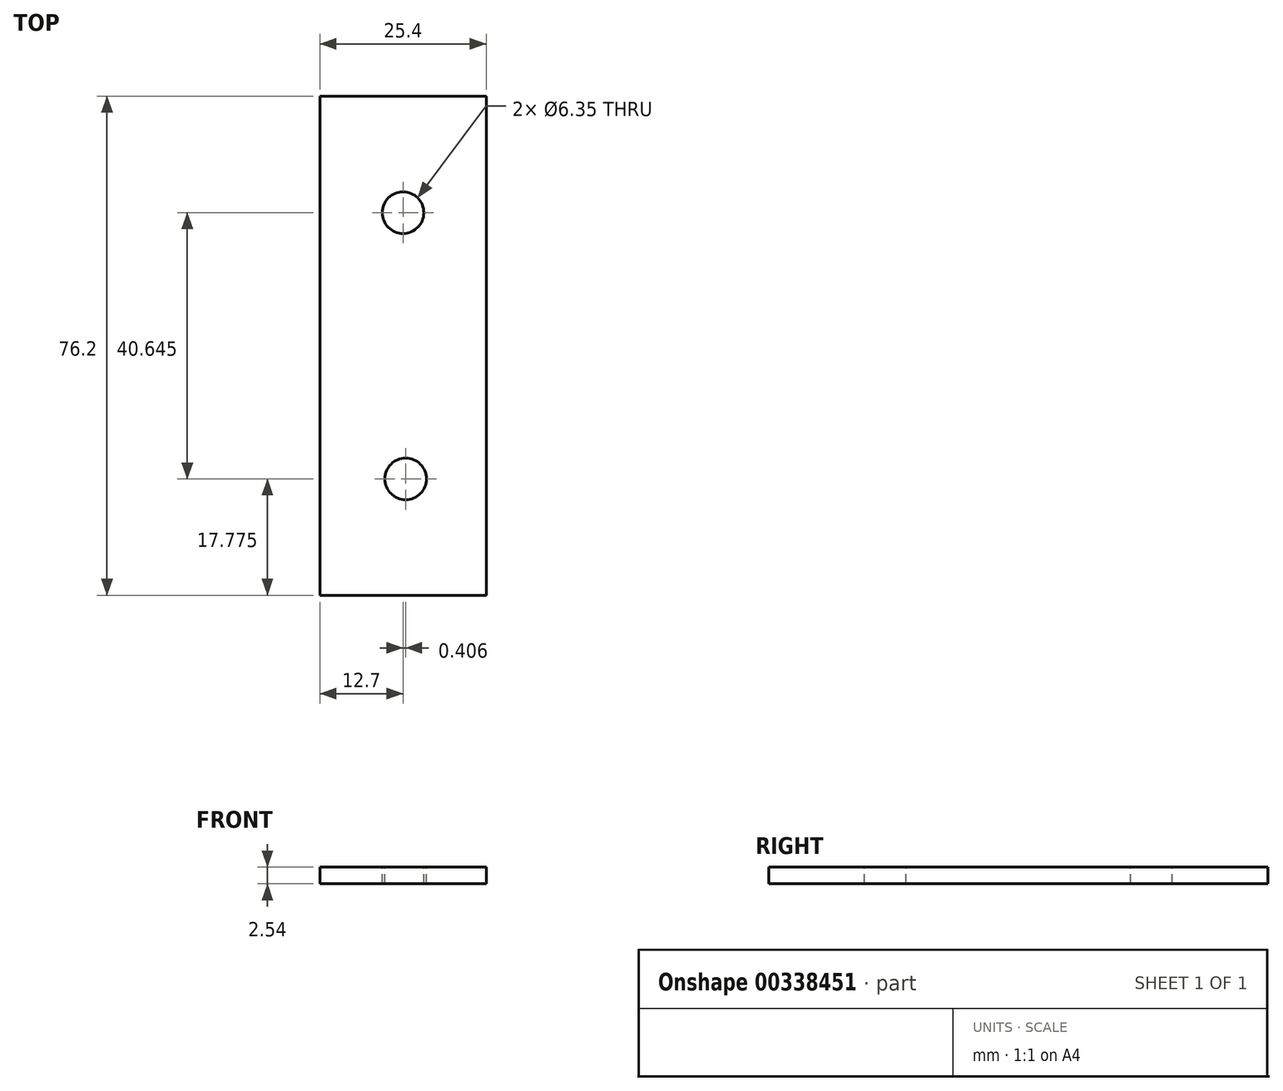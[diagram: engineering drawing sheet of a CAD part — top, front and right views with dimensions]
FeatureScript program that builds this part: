
annotation { "Feature Type Name" : "Feature", "Feature Type Description" : "" }
export const myFeature = defineFeature(function(context is Context, id is Id, definition is map)
    precondition{}
    {
        {
            var Q0;
            Q0=qCreatedBy(makeId("Top.planeOp"),FACE);
            var sketch = newSketch(context, id + "F0", { "sketchPlane" : qUnion([Q0])});
            skLineSegment(sketch, "E0.bottom", {"start": v(0, 0) * mm, "end": v(25.4, 0) * mm});
            skLineSegment(sketch, "E0.top", {"start": v(0, 76.2) * mm, "end": v(25.4, 76.2) * mm});
            skLineSegment(sketch, "E0.left", {"start": v(0, 0) * mm, "end": v(0, 76.2) * mm});
            skLineSegment(sketch, "E0.right", {"start": v(25.4, 0) * mm, "end": v(25.4, 76.2) * mm});
            skSolve(sketch);
        }
        {
            var Q0;
            Q0=makeQuery(id+"F0.imprint","IMPRINT",FACE,{"disambiguationData":[TD([[makeQuery(id+"F0.imprint","IMPRINT",EDGE,{"derivedFrom":sQuery(id+"F0.wireOp",EDGE,"E0.bottom")}),1.0]])]});
            extrude(context, id + "F1", {"entities" : qUnion([Q0]), "depth" : 2.54 * mm});
        }
        {
            var Q0;
            Q0=makeQuery(id+"F1.opExtrude","CAP_FACE",FACE,{"disambiguationData":[OSD([sQuery(id+"F0.wireOp",EDGE,"E0.bottom"),sQuery(id+"F0.wireOp",EDGE,"E0.top"),sQuery(id+"F0.wireOp",EDGE,"E0.left"),sQuery(id+"F0.wireOp",EDGE,"E0.right")])],"isStart":false});
            var sketch = newSketch(context, id + "F2", { "sketchPlane" : qUnion([Q0])});
            skPoint(sketch, "E1", {"position": v(12.7, 58.42) * mm});
            skPoint(sketch, "E1.positionSnap0", {"position": v(12.7, 0) * mm});
            skPoint(sketch, "E2", {"position": v(13.1, 17.78) * mm});
            skCircle(sketch, "E3", {"center": v(12.7, 58.42) * mm, "radius": 3.18 * mm});
            skCircle(sketch, "E4", {"center": v(13.1, 17.78) * mm, "radius": 3.18 * mm});
            skSolve(sketch);
        }
        {
            var Q0;
            Q0=makeQuery(id+"F2.imprint","IMPRINT",FACE,{"disambiguationData":[TD([[makeQuery(id+"F2.imprint","IMPRINT",EDGE,{"derivedFrom":sQuery(id+"F2.wireOp",EDGE,"E3")}),1.0]])]});
            var Q1;
            Q1=makeQuery(id+"F2.imprint","IMPRINT",FACE,{"disambiguationData":[TD([[makeQuery(id+"F2.imprint","IMPRINT",EDGE,{"derivedFrom":sQuery(id+"F2.wireOp",EDGE,"E4")}),1.0]])]});
            extrude(context, id + "F3", {"entities" : qUnion([Q0, Q1]), "operationType" : NewBodyOperationType.REMOVE, "oppositeDirection" : true, "depth" : 25.4 * mm});
        }
    });
